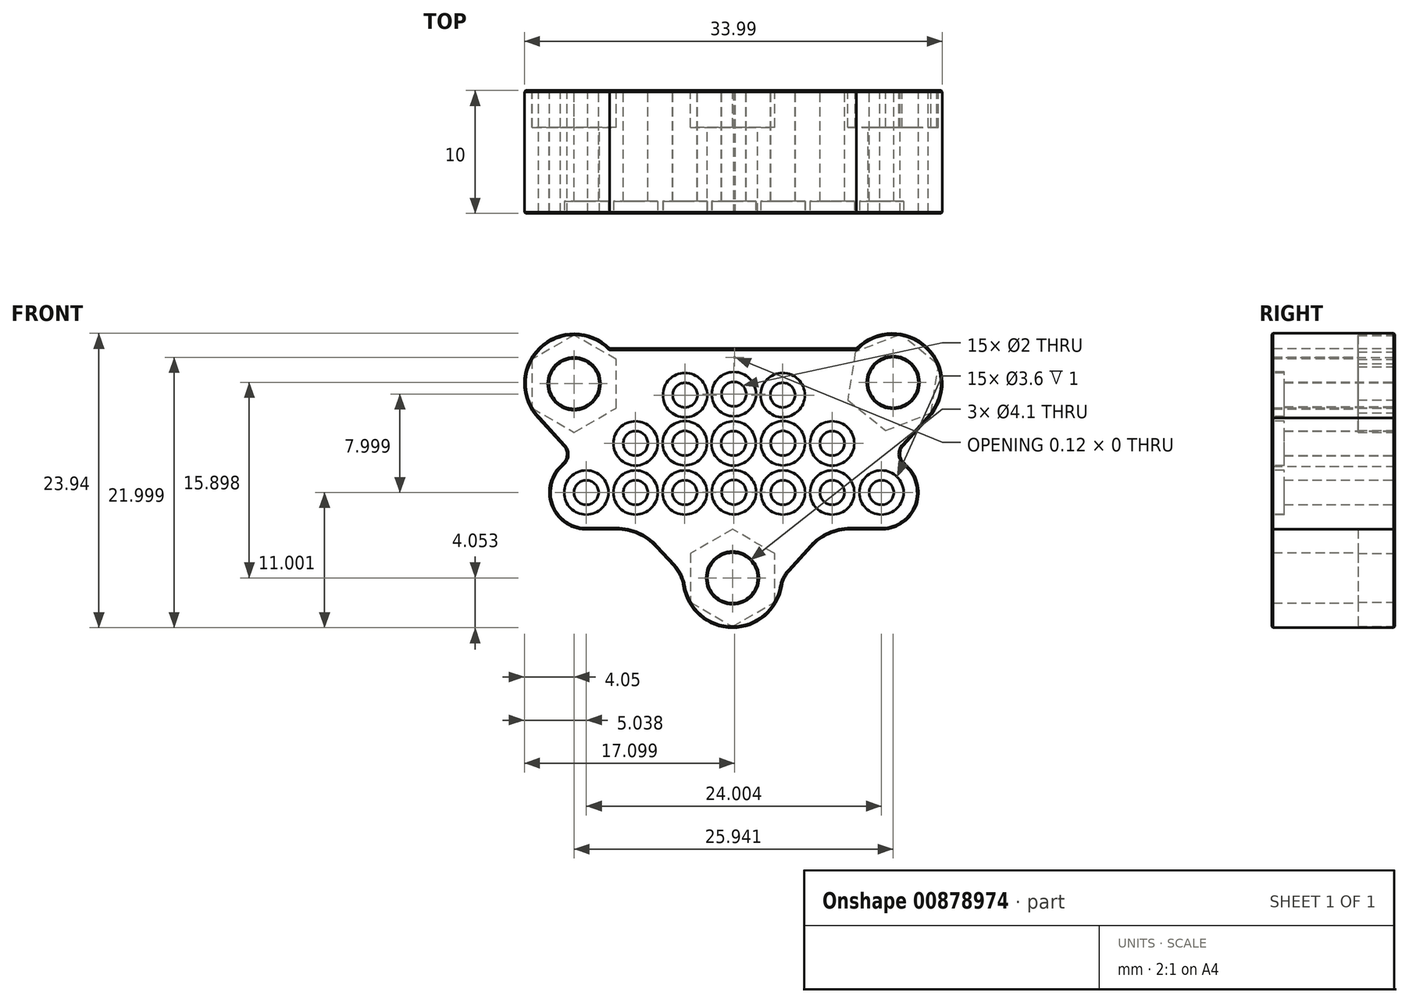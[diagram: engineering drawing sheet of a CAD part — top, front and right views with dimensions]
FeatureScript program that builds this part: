
annotation { "Feature Type Name" : "Feature", "Feature Type Description" : "" }
export const myFeature = defineFeature(function(context is Context, id is Id, definition is map)
    precondition{}
    {
        {
            var Q0;
            Q0=qCreatedBy(makeId("Front.planeOp"),FACE);
            var sketch = newSketch(context, id + "F0", { "sketchPlane" : qUnion([Q0])});
            skLineSegment(sketch, "E0", {"start": v(0, 0) * mm, "end": v(12, 0) * mm, "construction": true});
            skLineSegment(sketch, "E1.0", {"start": v(0, -4) * mm, "end": v(12, -4) * mm, "construction": true});
            skLineSegment(sketch, "E2", {"start": v(0, 4) * mm, "end": v(0, -4) * mm, "construction": true});
            skLineSegment(sketch, "E3.0", {"start": v(4, 4) * mm, "end": v(4, -4) * mm, "construction": true});
            skLineSegment(sketch, "E4.0", {"start": v(8, 4) * mm, "end": v(8, -4) * mm, "construction": true});
            skLineSegment(sketch, "E5.0", {"start": v(12, 0) * mm, "end": v(12, -4) * mm, "construction": true});
            skLineSegment(sketch, "E6.0", {"start": v(0, 4) * mm, "end": v(8, 4) * mm, "construction": true});
            skCircle(sketch, "E7", {"center": v(0, 4) * mm, "radius": 1 * mm});
            skCircle(sketch, "E8", {"center": v(3.97, 3.92) * mm, "radius": 1 * mm});
            skCircle(sketch, "E9", {"center": v(-0.03, 0) * mm, "radius": 1 * mm});
            skCircle(sketch, "E10", {"center": v(4, 0) * mm, "radius": 1 * mm});
            skCircle(sketch, "E11", {"center": v(8, 0) * mm, "radius": 1 * mm});
            skCircle(sketch, "E12", {"center": v(0, -3.98) * mm, "radius": 1 * mm});
            skCircle(sketch, "E13", {"center": v(4, -4) * mm, "radius": 1 * mm});
            skCircle(sketch, "E14", {"center": v(8, -4) * mm, "radius": 1 * mm});
            skCircle(sketch, "E15", {"center": v(12, -4) * mm, "radius": 1 * mm});
            skArc(sketch, "E16.0", {"start": v(11.88, -7) * mm, "mid": v(14.75, -5.2) * mm, "end": v(14.1, -1.86) * mm});
            skLineSegment(sketch, "E17", {"start": v(0, 7) * mm, "end": v(0.12, 7) * mm});
            skLineSegment(sketch, "E18", {"start": v(12.12, -7) * mm, "end": v(9.45, -7) * mm});
            skArc(sketch, "E19.trimOffspring", {"start": v(0.12, 7) * mm, "mid": v(0.06, 7) * mm, "end": v(0, 7) * mm});
            skCircle(sketch, "E20.MirrorC", {"center": v(-4, -4) * mm, "radius": 1 * mm});
            skCircle(sketch, "E21.MirrorC", {"center": v(-8, -4) * mm, "radius": 1 * mm});
            skCircle(sketch, "E22.MirrorC", {"center": v(-12, -4) * mm, "radius": 1 * mm});
            skLineSegment(sketch, "E23.MirrorCS", {"start": v(-4, 4) * mm, "end": v(-4, -4) * mm, "construction": true});
            skCircle(sketch, "E24.MirrorC", {"center": v(-4, 0) * mm, "radius": 1 * mm});
            skLineSegment(sketch, "E25.MirrorCS", {"start": v(-12, 0) * mm, "end": v(-12, -4) * mm, "construction": true});
            skLineSegment(sketch, "E26.MirrorCS", {"start": v(-8, 4) * mm, "end": v(-8, -4) * mm, "construction": true});
            skCircle(sketch, "E27.MirrorC", {"center": v(-3.97, 3.92) * mm, "radius": 1 * mm});
            skCircle(sketch, "E28.MirrorC", {"center": v(-8, 0) * mm, "radius": 1 * mm});
            skArc(sketch, "E29.MirrorCS", {"start": v(-11.88, -7) * mm, "mid": v(-14.75, -5.2) * mm, "end": v(-14.1, -1.86) * mm});
            skLineSegment(sketch, "E30.MirrorCS", {"start": v(-12.12, -7) * mm, "end": v(-9.54, -7) * mm});
            skPoint(sketch, "E31.orphan", {"position": v(3, -4.1) * mm});
            skPoint(sketch, "E32.0.end.orphan", {"position": v(3, -3.88) * mm});
            skPoint(sketch, "E33.MirrorCS.end.orphan", {"position": v(-3, -3.88) * mm});
            skPoint(sketch, "E33.MirrorCS.start.orphan", {"position": v(-3, -4.1) * mm});
            skLineSegment(sketch, "E34.0", {"start": v(12.1, -11) * mm, "end": v(0, -10.98) * mm});
            skCircle(sketch, "E35", {"center": v(-12.99, 4.85) * mm, "radius": 2.05 * mm});
            skCircle(sketch, "E36", {"center": v(12.95, 4.95) * mm, "radius": 2.05 * mm});
            skCircle(sketch, "E37", {"center": v(-0.1, -10.95) * mm, "radius": 2.05 * mm});
            skArc(sketch, "E38.0", {"start": v(-4.1, -11.59) * mm, "mid": v(-0.13, -15) * mm, "end": v(3.88, -11.63) * mm});
            skLineSegment(sketch, "E39", {"start": v(-10.1, 7.7) * mm, "end": v(9.97, 7.7) * mm});
            skLineSegment(sketch, "E40", {"start": v(-15.87, 2.02) * mm, "end": v(-13.82, -0.22) * mm});
            skLineSegment(sketch, "E41", {"start": v(4.5, -10.37) * mm, "end": v(6.32, -8.37) * mm});
            skLineSegment(sketch, "E42.trimOffspring", {"start": v(-13.84, -1.58) * mm, "end": v(-14.1, -1.86) * mm});
            skLineSegment(sketch, "E43.trimOffspring", {"start": v(-6.32, -8.4) * mm, "end": v(-4.88, -9.98) * mm});
            skArc(sketch, "E44.trimOffspring", {"start": v(-10.1, 7.7) * mm, "mid": v(-15.83, 7.75) * mm, "end": v(-15.87, 2.02) * mm});
            skPoint(sketch, "E45.MirrorCS.end.orphan", {"position": v(-4.03, 6.92) * mm});
            skPoint(sketch, "E45.MirrorCS.start.orphan", {"position": v(-6.26, 5.86) * mm});
            skPoint(sketch, "E46.MirrorCS.start.orphan", {"position": v(0, 7) * mm});
            skPoint(sketch, "E47.trimOffspring.end.orphan", {"position": v(4.03, 6.92) * mm});
            skPoint(sketch, "E48.orphan", {"position": v(6.26, 5.86) * mm});
            skArc(sketch, "E49.trimOffspring", {"start": v(15.81, 2.07) * mm, "mid": v(15.7, 7.8) * mm, "end": v(9.97, 7.7) * mm});
            skLineSegment(sketch, "E50.trimOffspring", {"start": v(13.8, -1.57) * mm, "end": v(14.1, -1.86) * mm});
            skLineSegment(sketch, "E51.trimOffspring", {"start": v(13.77, -0.18) * mm, "end": v(15.81, 2.07) * mm});
            skPoint(sketch, "E52.trimOffspring.end.orphan", {"position": v(0, -6.98) * mm});
            skPoint(sketch, "E53.0.start.orphan", {"position": v(-9.07, 8.7) * mm});
            skPoint(sketch, "E54.trimOffspring.end.orphan", {"position": v(-16.91, 1) * mm});
            skPoint(sketch, "E55.visualSharp", {"position": v(-13.2, -0.9) * mm});
            skArc(sketch, "E55.filletArc", {"start": v(-13.84, -1.58) * mm, "mid": v(-13.56, -0.9) * mm, "end": v(-13.82, -0.22) * mm});
            skPoint(sketch, "E56.visualSharp", {"position": v(-7.62, -6.99) * mm});
            skArc(sketch, "E56.filletArc", {"start": v(-6.32, -8.4) * mm, "mid": v(-7.78, -7.36) * mm, "end": v(-9.54, -7) * mm});
            skPoint(sketch, "E57.visualSharp", {"position": v(-4.15, -10.78) * mm});
            skArc(sketch, "E57.filletArc", {"start": v(-4.1, -11.59) * mm, "mid": v(-4.38, -10.73) * mm, "end": v(-4.88, -9.98) * mm});
            skPoint(sketch, "E58.visualSharp", {"position": v(13.12, -0.9) * mm});
            skArc(sketch, "E58.filletArc", {"start": v(13.77, -0.18) * mm, "mid": v(13.5, -0.88) * mm, "end": v(13.8, -1.57) * mm});
            skPoint(sketch, "E59.visualSharp", {"position": v(7.57, -6.99) * mm});
            skArc(sketch, "E59.filletArc", {"start": v(9.45, -7) * mm, "mid": v(7.73, -7.35) * mm, "end": v(6.32, -8.37) * mm});
            skPoint(sketch, "E60.visualSharp", {"position": v(3.94, -10.98) * mm});
            skArc(sketch, "E60.filletArc", {"start": v(4.5, -10.37) * mm, "mid": v(4.1, -10.96) * mm, "end": v(3.88, -11.63) * mm});
            skSolve(sketch);
        }
        {
            var Q0;
            Q0 = qSketchRegion(id + "F0", true);
            extrude(context, id + "F1", {"entities" : qUnion([Q0]), "depth" : 10 * mm, "offsetDistance" : 25 * mm});
        }
        {
            var Q0;
            Q0=makeQuery(id+"F1.opExtrude","CAP_FACE",FACE,{"disambiguationData":[OSD([sQuery(id+"F0.wireOp",EDGE,"E7"),sQuery(id+"F0.wireOp",EDGE,"E8"),sQuery(id+"F0.wireOp",EDGE,"E9"),sQuery(id+"F0.wireOp",EDGE,"E10"),sQuery(id+"F0.wireOp",EDGE,"E11"),sQuery(id+"F0.wireOp",EDGE,"E12"),sQuery(id+"F0.wireOp",EDGE,"E13"),sQuery(id+"F0.wireOp",EDGE,"E14"),sQuery(id+"F0.wireOp",EDGE,"E15"),sQuery(id+"F0.wireOp",EDGE,"E16.0"),sQuery(id+"F0.wireOp",EDGE,"E17"),sQuery(id+"F0.wireOp",EDGE,"E18"),sQuery(id+"F0.wireOp",EDGE,"E19.trimOffspring"),sQuery(id+"F0.wireOp",EDGE,"E20.MirrorC"),sQuery(id+"F0.wireOp",EDGE,"E21.MirrorC"),sQuery(id+"F0.wireOp",EDGE,"E22.MirrorC"),sQuery(id+"F0.wireOp",EDGE,"E24.MirrorC"),sQuery(id+"F0.wireOp",EDGE,"E27.MirrorC"),sQuery(id+"F0.wireOp",EDGE,"E28.MirrorC"),sQuery(id+"F0.wireOp",EDGE,"E29.MirrorCS"),sQuery(id+"F0.wireOp",EDGE,"E30.MirrorCS"),sQuery(id+"F0.wireOp",EDGE,"E35"),sQuery(id+"F0.wireOp",EDGE,"E36"),sQuery(id+"F0.wireOp",EDGE,"E37"),sQuery(id+"F0.wireOp",EDGE,"E38.0"),sQuery(id+"F0.wireOp",EDGE,"E39"),sQuery(id+"F0.wireOp",EDGE,"E40"),sQuery(id+"F0.wireOp",EDGE,"E41"),sQuery(id+"F0.wireOp",EDGE,"E42.trimOffspring"),sQuery(id+"F0.wireOp",EDGE,"E43.trimOffspring"),sQuery(id+"F0.wireOp",EDGE,"E44.trimOffspring"),sQuery(id+"F0.wireOp",EDGE,"E49.trimOffspring"),sQuery(id+"F0.wireOp",EDGE,"E50.trimOffspring"),sQuery(id+"F0.wireOp",EDGE,"E51.trimOffspring"),sQuery(id+"F0.wireOp",EDGE,"E55.filletArc"),sQuery(id+"F0.wireOp",EDGE,"E56.filletArc"),sQuery(id+"F0.wireOp",EDGE,"E57.filletArc"),sQuery(id+"F0.wireOp",EDGE,"E58.filletArc"),sQuery(id+"F0.wireOp",EDGE,"E59.filletArc"),sQuery(id+"F0.wireOp",EDGE,"E60.filletArc")])],"isStart":false});
            var sketch = newSketch(context, id + "F2", { "sketchPlane" : qUnion([Q0])});
            skCircle(sketch, "E61.0", {"center": v(-3.97, 3.92) * mm, "radius": 1.8 * mm});
            skLineSegment(sketch, "E62.0", {"start": v(9.78, -12) * mm, "end": v(11.8, -12) * mm});
            skLineSegment(sketch, "E62.1", {"start": v(8.65, -13.24) * mm, "end": v(9.78, -12) * mm});
            skArc(sketch, "E62.2", {"start": v(11.8, -12) * mm, "mid": v(18.5, -8.68) * mm, "end": v(19.53, -1.28) * mm});
            skArc(sketch, "E62.3", {"start": v(-8.93, -12.97) * mm, "mid": v(-0.25, -20) * mm, "end": v(8.65, -13.24) * mm});
            skLineSegment(sketch, "E62.4", {"start": v(-9.82, -12) * mm, "end": v(-8.93, -12.97) * mm});
            skLineSegment(sketch, "E62.5", {"start": v(-11.8, -12) * mm, "end": v(-9.82, -12) * mm});
            skArc(sketch, "E62.6", {"start": v(19.53, -1.28) * mm, "mid": v(19.96, 10.55) * mm, "end": v(8.31, 12.7) * mm});
            skLineSegment(sketch, "E62.7", {"start": v(8.31, 12.7) * mm, "end": v(-8.47, 12.7) * mm});
            skArc(sketch, "E62.8", {"start": v(-8.47, 12.7) * mm, "mid": v(-20.1, 10.46) * mm, "end": v(-19.56, -1.36) * mm});
            skArc(sketch, "E62.9", {"start": v(-19.56, -1.36) * mm, "mid": v(-18.46, -8.72) * mm, "end": v(-11.8, -12) * mm});
            skCircle(sketch, "E63.0", {"center": v(0, 4) * mm, "radius": 1.8 * mm});
            skCircle(sketch, "E64.0", {"center": v(3.97, 3.92) * mm, "radius": 1.8 * mm});
            skCircle(sketch, "E65.0", {"center": v(-8, 0) * mm, "radius": 1.8 * mm});
            skCircle(sketch, "E66.0", {"center": v(-4, 0) * mm, "radius": 1.8 * mm});
            skCircle(sketch, "E67.0", {"center": v(-0.03, 0) * mm, "radius": 1.8 * mm});
            skCircle(sketch, "E68.0", {"center": v(4, 0) * mm, "radius": 1.8 * mm});
            skCircle(sketch, "E69.0", {"center": v(8, 0) * mm, "radius": 1.8 * mm});
            skCircle(sketch, "E70.0", {"center": v(-12, -4) * mm, "radius": 1.8 * mm});
            skCircle(sketch, "E71.0", {"center": v(-8, -4) * mm, "radius": 1.8 * mm});
            skCircle(sketch, "E72.0", {"center": v(-4, -4) * mm, "radius": 1.8 * mm});
            skCircle(sketch, "E73.0", {"center": v(0, -3.98) * mm, "radius": 1.8 * mm});
            skCircle(sketch, "E74.0", {"center": v(4, -4) * mm, "radius": 1.8 * mm});
            skCircle(sketch, "E75.0", {"center": v(8, -4) * mm, "radius": 1.8 * mm});
            skCircle(sketch, "E76.0", {"center": v(12, -4) * mm, "radius": 1.8 * mm});
            skSolve(sketch);
        }
        {
            var Q0;
            Q0=makeQuery(id+"F2.imprint","IMPRINT",FACE,{"disambiguationData":[TD([[makeQuery(id+"F2.imprint","IMPRINT",EDGE,{"derivedFrom":sQuery(id+"F2.wireOp",EDGE,"E73.0")}),1.0]])]});
            var Q1;
            Q1=makeQuery(id+"F2.imprint","IMPRINT",FACE,{"disambiguationData":[TD([[makeQuery(id+"F2.imprint","IMPRINT",EDGE,{"derivedFrom":sQuery(id+"F2.wireOp",EDGE,"E76.0")}),1.0]])]});
            var Q2;
            Q2=makeQuery(id+"F2.imprint","IMPRINT",FACE,{"disambiguationData":[TD([[makeQuery(id+"F2.imprint","IMPRINT",EDGE,{"derivedFrom":sQuery(id+"F2.wireOp",EDGE,"E75.0")}),1.0]])]});
            var Q3;
            Q3=makeQuery(id+"F2.imprint","IMPRINT",FACE,{"disambiguationData":[TD([[makeQuery(id+"F2.imprint","IMPRINT",EDGE,{"derivedFrom":sQuery(id+"F2.wireOp",EDGE,"E74.0")}),1.0]])]});
            var Q4;
            Q4=makeQuery(id+"F2.imprint","IMPRINT",FACE,{"disambiguationData":[TD([[makeQuery(id+"F2.imprint","IMPRINT",EDGE,{"derivedFrom":sQuery(id+"F2.wireOp",EDGE,"E72.0")}),1.0]])]});
            var Q5;
            Q5=makeQuery(id+"F2.imprint","IMPRINT",FACE,{"disambiguationData":[TD([[makeQuery(id+"F2.imprint","IMPRINT",EDGE,{"derivedFrom":sQuery(id+"F2.wireOp",EDGE,"E71.0")}),1.0]])]});
            var Q6;
            Q6=makeQuery(id+"F2.imprint","IMPRINT",FACE,{"disambiguationData":[TD([[makeQuery(id+"F2.imprint","IMPRINT",EDGE,{"derivedFrom":sQuery(id+"F2.wireOp",EDGE,"E70.0")}),1.0]])]});
            var Q7;
            Q7=makeQuery(id+"F2.imprint","IMPRINT",FACE,{"disambiguationData":[TD([[makeQuery(id+"F2.imprint","IMPRINT",EDGE,{"derivedFrom":sQuery(id+"F2.wireOp",EDGE,"E65.0")}),1.0]])]});
            var Q8;
            Q8=makeQuery(id+"F2.imprint","IMPRINT",FACE,{"disambiguationData":[TD([[makeQuery(id+"F2.imprint","IMPRINT",EDGE,{"derivedFrom":sQuery(id+"F2.wireOp",EDGE,"E66.0")}),1.0]])]});
            var Q9;
            Q9=makeQuery(id+"F2.imprint","IMPRINT",FACE,{"disambiguationData":[TD([[makeQuery(id+"F2.imprint","IMPRINT",EDGE,{"derivedFrom":sQuery(id+"F2.wireOp",EDGE,"E67.0")}),1.0]])]});
            var Q10;
            Q10=makeQuery(id+"F2.imprint","IMPRINT",FACE,{"disambiguationData":[TD([[makeQuery(id+"F2.imprint","IMPRINT",EDGE,{"derivedFrom":sQuery(id+"F2.wireOp",EDGE,"E68.0")}),1.0]])]});
            var Q11;
            Q11=makeQuery(id+"F2.imprint","IMPRINT",FACE,{"disambiguationData":[TD([[makeQuery(id+"F2.imprint","IMPRINT",EDGE,{"derivedFrom":sQuery(id+"F2.wireOp",EDGE,"E69.0")}),1.0]])]});
            var Q12;
            Q12=makeQuery(id+"F2.imprint","IMPRINT",FACE,{"disambiguationData":[TD([[makeQuery(id+"F2.imprint","IMPRINT",EDGE,{"derivedFrom":sQuery(id+"F2.wireOp",EDGE,"E64.0")}),1.0]])]});
            var Q13;
            Q13=makeQuery(id+"F2.imprint","IMPRINT",FACE,{"disambiguationData":[TD([[makeQuery(id+"F2.imprint","IMPRINT",EDGE,{"derivedFrom":sQuery(id+"F2.wireOp",EDGE,"E63.0")}),1.0]])]});
            var Q14;
            Q14=makeQuery(id+"F2.imprint","IMPRINT",FACE,{"disambiguationData":[TD([[makeQuery(id+"F2.imprint","IMPRINT",EDGE,{"derivedFrom":sQuery(id+"F2.wireOp",EDGE,"E61.0")}),1.0]])]});
            extrude(context, id + "F3", {"entities" : qUnion([Q0, Q1, Q2, Q3, Q4, Q5, Q6, Q7, Q8, Q9, Q10, Q11, Q12, Q13, Q14]), "operationType" : NewBodyOperationType.REMOVE, "oppositeDirection" : true, "depth" : 1 * mm, "offsetDistance" : 25 * mm});
        }
        {
            var Q0;
            Q0=makeQuery(id+"F1.opExtrude","CAP_EDGE",EDGE,{"disambiguationData":[OSD([sQuery(id+"F0.wireOp",EDGE,"E39")])],"isStart":false});
            var Q1;
            Q1=makeQuery(id+"F1.opExtrude","CAP_EDGE",EDGE,{"disambiguationData":[OSD([sQuery(id+"F0.wireOp",EDGE,"E49.trimOffspring")])],"isStart":false});
            var Q2;
            Q2=makeQuery(id+"F1.opExtrude","CAP_EDGE",EDGE,{"disambiguationData":[OSD([sQuery(id+"F0.wireOp",EDGE,"E36")])],"isStart":false});
            var Q3;
            Q3=makeQuery(id+"F1.opExtrude","CAP_EDGE",EDGE,{"disambiguationData":[OSD([sQuery(id+"F0.wireOp",EDGE,"E51.trimOffspring")])],"isStart":false});
            var Q4;
            Q4=makeQuery(id+"F1.opExtrude","CAP_EDGE",EDGE,{"disambiguationData":[OSD([sQuery(id+"F0.wireOp",EDGE,"E58.filletArc")])],"isStart":false});
            var Q5;
            Q5=makeQuery(id+"F1.opExtrude","CAP_EDGE",EDGE,{"disambiguationData":[OSD([sQuery(id+"F0.wireOp",EDGE,"E50.trimOffspring")])],"isStart":false});
            var Q6;
            Q6=makeQuery(id+"F1.opExtrude","CAP_EDGE",EDGE,{"disambiguationData":[OSD([sQuery(id+"F0.wireOp",EDGE,"E16.0")])],"isStart":false});
            var Q7;
            Q7=makeQuery(id+"F1.opExtrude","CAP_EDGE",EDGE,{"disambiguationData":[OSD([sQuery(id+"F0.wireOp",EDGE,"E18")])],"isStart":false});
            var Q8;
            Q8=makeQuery(id+"F1.opExtrude","CAP_EDGE",EDGE,{"disambiguationData":[OSD([sQuery(id+"F0.wireOp",EDGE,"E59.filletArc")])],"isStart":false});
            var Q9;
            Q9=makeQuery(id+"F1.opExtrude","CAP_EDGE",EDGE,{"disambiguationData":[OSD([sQuery(id+"F0.wireOp",EDGE,"E41")])],"isStart":false});
            var Q10;
            Q10=makeQuery(id+"F1.opExtrude","CAP_EDGE",EDGE,{"disambiguationData":[OSD([sQuery(id+"F0.wireOp",EDGE,"E60.filletArc")])],"isStart":false});
            var Q11;
            Q11=makeQuery(id+"F1.opExtrude","CAP_EDGE",EDGE,{"disambiguationData":[OSD([sQuery(id+"F0.wireOp",EDGE,"E38.0")])],"isStart":false});
            var Q12;
            Q12=makeQuery(id+"F1.opExtrude","CAP_EDGE",EDGE,{"disambiguationData":[OSD([sQuery(id+"F0.wireOp",EDGE,"E57.filletArc")])],"isStart":false});
            var Q13;
            Q13=makeQuery(id+"F1.opExtrude","CAP_EDGE",EDGE,{"disambiguationData":[OSD([sQuery(id+"F0.wireOp",EDGE,"E43.trimOffspring")])],"isStart":false});
            var Q14;
            Q14=makeQuery(id+"F1.opExtrude","CAP_EDGE",EDGE,{"disambiguationData":[OSD([sQuery(id+"F0.wireOp",EDGE,"E56.filletArc")])],"isStart":false});
            var Q15;
            Q15=makeQuery(id+"F1.opExtrude","CAP_EDGE",EDGE,{"disambiguationData":[OSD([sQuery(id+"F0.wireOp",EDGE,"E30.MirrorCS")])],"isStart":false});
            var Q16;
            Q16=makeQuery(id+"F1.opExtrude","CAP_EDGE",EDGE,{"disambiguationData":[OSD([sQuery(id+"F0.wireOp",EDGE,"E37")])],"isStart":false});
            var Q17;
            Q17=makeQuery(id+"F1.opExtrude","CAP_EDGE",EDGE,{"disambiguationData":[OSD([sQuery(id+"F0.wireOp",EDGE,"E29.MirrorCS")])],"isStart":false});
            var Q18;
            Q18=makeQuery(id+"F1.opExtrude","CAP_EDGE",EDGE,{"disambiguationData":[OSD([sQuery(id+"F0.wireOp",EDGE,"E42.trimOffspring")])],"isStart":false});
            var Q19;
            Q19=makeQuery(id+"F1.opExtrude","CAP_EDGE",EDGE,{"disambiguationData":[OSD([sQuery(id+"F0.wireOp",EDGE,"E55.filletArc")])],"isStart":false});
            var Q20;
            Q20=makeQuery(id+"F1.opExtrude","CAP_EDGE",EDGE,{"disambiguationData":[OSD([sQuery(id+"F0.wireOp",EDGE,"E40")])],"isStart":false});
            var Q21;
            Q21=makeQuery(id+"F1.opExtrude","CAP_EDGE",EDGE,{"disambiguationData":[OSD([sQuery(id+"F0.wireOp",EDGE,"E44.trimOffspring")])],"isStart":false});
            var Q22;
            Q22=makeQuery(id+"F1.opExtrude","CAP_EDGE",EDGE,{"disambiguationData":[OSD([sQuery(id+"F0.wireOp",EDGE,"E35")])],"isStart":false});
            var Q23;
            Q23=makeQuery(id+"F3.boolean.opBoolean","COPY",EDGE,{"derivedFrom":makeQuery(id+"F3.opExtrude","CAP_EDGE",EDGE,{"disambiguationData":[OSD([sQuery(id+"F2.wireOp",EDGE,"E61.0")])],"isStart":true})});
            var Q24;
            Q24=makeQuery(id+"F3.boolean.opBoolean","COPY",EDGE,{"derivedFrom":makeQuery(id+"F3.opExtrude","CAP_EDGE",EDGE,{"disambiguationData":[OSD([sQuery(id+"F2.wireOp",EDGE,"E65.0")])],"isStart":true})});
            var Q25;
            Q25=makeQuery(id+"F3.boolean.opBoolean","COPY",EDGE,{"derivedFrom":makeQuery(id+"F3.opExtrude","CAP_EDGE",EDGE,{"disambiguationData":[OSD([sQuery(id+"F2.wireOp",EDGE,"E70.0")])],"isStart":true})});
            var Q26;
            Q26=makeQuery(id+"F3.boolean.opBoolean","COPY",EDGE,{"derivedFrom":makeQuery(id+"F3.opExtrude","CAP_EDGE",EDGE,{"disambiguationData":[OSD([sQuery(id+"F2.wireOp",EDGE,"E71.0")])],"isStart":true})});
            var Q27;
            Q27=makeQuery(id+"F3.boolean.opBoolean","COPY",EDGE,{"derivedFrom":makeQuery(id+"F3.opExtrude","CAP_EDGE",EDGE,{"disambiguationData":[OSD([sQuery(id+"F2.wireOp",EDGE,"E72.0")])],"isStart":true})});
            var Q28;
            Q28=makeQuery(id+"F3.boolean.opBoolean","COPY",EDGE,{"derivedFrom":makeQuery(id+"F3.opExtrude","CAP_EDGE",EDGE,{"disambiguationData":[OSD([sQuery(id+"F2.wireOp",EDGE,"E66.0")])],"isStart":true})});
            var Q29;
            Q29=makeQuery(id+"F3.boolean.opBoolean","COPY",EDGE,{"derivedFrom":makeQuery(id+"F3.opExtrude","CAP_EDGE",EDGE,{"disambiguationData":[OSD([sQuery(id+"F2.wireOp",EDGE,"E63.0")])],"isStart":true})});
            var Q30;
            Q30=makeQuery(id+"F3.boolean.opBoolean","COPY",EDGE,{"derivedFrom":makeQuery(id+"F3.opExtrude","CAP_EDGE",EDGE,{"disambiguationData":[OSD([sQuery(id+"F2.wireOp",EDGE,"E67.0")])],"isStart":true})});
            var Q31;
            Q31=makeQuery(id+"F3.boolean.opBoolean","COPY",EDGE,{"derivedFrom":makeQuery(id+"F3.opExtrude","CAP_EDGE",EDGE,{"disambiguationData":[OSD([sQuery(id+"F2.wireOp",EDGE,"E73.0")])],"isStart":true})});
            var Q32;
            Q32=makeQuery(id+"F3.boolean.opBoolean","COPY",EDGE,{"derivedFrom":makeQuery(id+"F3.opExtrude","CAP_EDGE",EDGE,{"disambiguationData":[OSD([sQuery(id+"F2.wireOp",EDGE,"E74.0")])],"isStart":true})});
            var Q33;
            Q33=makeQuery(id+"F3.boolean.opBoolean","COPY",EDGE,{"derivedFrom":makeQuery(id+"F3.opExtrude","CAP_EDGE",EDGE,{"disambiguationData":[OSD([sQuery(id+"F2.wireOp",EDGE,"E75.0")])],"isStart":true})});
            var Q34;
            Q34=makeQuery(id+"F3.boolean.opBoolean","COPY",EDGE,{"derivedFrom":makeQuery(id+"F3.opExtrude","CAP_EDGE",EDGE,{"disambiguationData":[OSD([sQuery(id+"F2.wireOp",EDGE,"E76.0")])],"isStart":true})});
            var Q35;
            Q35=makeQuery(id+"F3.boolean.opBoolean","COPY",EDGE,{"derivedFrom":makeQuery(id+"F3.opExtrude","CAP_EDGE",EDGE,{"disambiguationData":[OSD([sQuery(id+"F2.wireOp",EDGE,"E69.0")])],"isStart":true})});
            var Q36;
            Q36=makeQuery(id+"F3.boolean.opBoolean","COPY",EDGE,{"derivedFrom":makeQuery(id+"F3.opExtrude","CAP_EDGE",EDGE,{"disambiguationData":[OSD([sQuery(id+"F2.wireOp",EDGE,"E68.0")])],"isStart":true})});
            var Q37;
            Q37=makeQuery(id+"F3.boolean.opBoolean","COPY",EDGE,{"derivedFrom":makeQuery(id+"F3.opExtrude","CAP_EDGE",EDGE,{"disambiguationData":[OSD([sQuery(id+"F2.wireOp",EDGE,"E64.0")])],"isStart":true})});
            chamfer(context, id + "F4", {"entities" : qUnion([Q0, Q1, Q2, Q3, Q4, Q5, Q6, Q7, Q8, Q9, Q10, Q11, Q12, Q13, Q14, Q15, Q16, Q17, Q18, Q19, Q20, Q21, Q22, Q23, Q24, Q25, Q26, Q27, Q28, Q29, Q30, Q31, Q32, Q33, Q34, Q35, Q36, Q37]), "width" : 0.1 * mm, "tangentPropagation" : true});
        }
        {
            var Q0;
            Q0=makeQuery(id+"F1.opExtrude","CAP_EDGE",EDGE,{"disambiguationData":[OSD([sQuery(id+"F0.wireOp",EDGE,"E39")])],"isStart":true});
            var Q1;
            Q1=makeQuery(id+"F1.opExtrude","CAP_EDGE",EDGE,{"disambiguationData":[OSD([sQuery(id+"F0.wireOp",EDGE,"E44.trimOffspring")])],"isStart":true});
            var Q2;
            Q2=makeQuery(id+"F1.opExtrude","CAP_EDGE",EDGE,{"disambiguationData":[OSD([sQuery(id+"F0.wireOp",EDGE,"E40")])],"isStart":true});
            var Q3;
            Q3=makeQuery(id+"F1.opExtrude","CAP_EDGE",EDGE,{"disambiguationData":[OSD([sQuery(id+"F0.wireOp",EDGE,"E35")])],"isStart":true});
            var Q4;
            Q4=makeQuery(id+"F1.opExtrude","CAP_EDGE",EDGE,{"disambiguationData":[OSD([sQuery(id+"F0.wireOp",EDGE,"E36")])],"isStart":true});
            var Q5;
            Q5=makeQuery(id+"F1.opExtrude","CAP_EDGE",EDGE,{"disambiguationData":[OSD([sQuery(id+"F0.wireOp",EDGE,"E37")])],"isStart":true});
            var Q6;
            Q6=makeQuery(id+"F1.opExtrude","CAP_EDGE",EDGE,{"disambiguationData":[OSD([sQuery(id+"F0.wireOp",EDGE,"E29.MirrorCS")])],"isStart":true});
            var Q7;
            Q7=makeQuery(id+"F1.opExtrude","CAP_EDGE",EDGE,{"disambiguationData":[OSD([sQuery(id+"F0.wireOp",EDGE,"E55.filletArc")])],"isStart":true});
            var Q8;
            Q8=makeQuery(id+"F1.opExtrude","CAP_EDGE",EDGE,{"disambiguationData":[OSD([sQuery(id+"F0.wireOp",EDGE,"E30.MirrorCS")])],"isStart":true});
            var Q9;
            Q9=makeQuery(id+"F1.opExtrude","CAP_EDGE",EDGE,{"disambiguationData":[OSD([sQuery(id+"F0.wireOp",EDGE,"E56.filletArc")])],"isStart":true});
            var Q10;
            Q10=makeQuery(id+"F1.opExtrude","CAP_EDGE",EDGE,{"disambiguationData":[OSD([sQuery(id+"F0.wireOp",EDGE,"E43.trimOffspring")])],"isStart":true});
            var Q11;
            Q11=makeQuery(id+"F1.opExtrude","CAP_EDGE",EDGE,{"disambiguationData":[OSD([sQuery(id+"F0.wireOp",EDGE,"E57.filletArc")])],"isStart":true});
            var Q12;
            Q12=makeQuery(id+"F1.opExtrude","CAP_EDGE",EDGE,{"disambiguationData":[OSD([sQuery(id+"F0.wireOp",EDGE,"E38.0")])],"isStart":true});
            var Q13;
            Q13=makeQuery(id+"F1.opExtrude","CAP_EDGE",EDGE,{"disambiguationData":[OSD([sQuery(id+"F0.wireOp",EDGE,"E49.trimOffspring")])],"isStart":true});
            var Q14;
            Q14=makeQuery(id+"F1.opExtrude","CAP_EDGE",EDGE,{"disambiguationData":[OSD([sQuery(id+"F0.wireOp",EDGE,"E51.trimOffspring")])],"isStart":true});
            var Q15;
            Q15=makeQuery(id+"F1.opExtrude","CAP_EDGE",EDGE,{"disambiguationData":[OSD([sQuery(id+"F0.wireOp",EDGE,"E58.filletArc")])],"isStart":true});
            var Q16;
            Q16=makeQuery(id+"F1.opExtrude","CAP_EDGE",EDGE,{"disambiguationData":[OSD([sQuery(id+"F0.wireOp",EDGE,"E16.0")])],"isStart":true});
            var Q17;
            Q17=makeQuery(id+"F1.opExtrude","CAP_EDGE",EDGE,{"disambiguationData":[OSD([sQuery(id+"F0.wireOp",EDGE,"E18")])],"isStart":true});
            var Q18;
            Q18=makeQuery(id+"F1.opExtrude","CAP_EDGE",EDGE,{"disambiguationData":[OSD([sQuery(id+"F0.wireOp",EDGE,"E59.filletArc")])],"isStart":true});
            var Q19;
            Q19=makeQuery(id+"F1.opExtrude","CAP_EDGE",EDGE,{"disambiguationData":[OSD([sQuery(id+"F0.wireOp",EDGE,"E50.trimOffspring")])],"isStart":true});
            var Q20;
            Q20=makeQuery(id+"F1.opExtrude","CAP_EDGE",EDGE,{"disambiguationData":[OSD([sQuery(id+"F0.wireOp",EDGE,"E41")])],"isStart":true});
            var Q21;
            Q21=makeQuery(id+"F1.opExtrude","CAP_EDGE",EDGE,{"disambiguationData":[OSD([sQuery(id+"F0.wireOp",EDGE,"E60.filletArc")])],"isStart":true});
            chamfer(context, id + "F5", {"entities" : qUnion([Q0, Q1, Q2, Q3, Q4, Q5, Q6, Q7, Q8, Q9, Q10, Q11, Q12, Q13, Q14, Q15, Q16, Q17, Q18, Q19, Q20, Q21]), "width" : 0.1 * mm, "tangentPropagation" : true});
        }
        {
            var Q0;
            Q0=makeQuery(id+"F1.opExtrude","CAP_FACE",FACE,{"disambiguationData":[OSD([sQuery(id+"F0.wireOp",EDGE,"E7"),sQuery(id+"F0.wireOp",EDGE,"E8"),sQuery(id+"F0.wireOp",EDGE,"E9"),sQuery(id+"F0.wireOp",EDGE,"E10"),sQuery(id+"F0.wireOp",EDGE,"E11"),sQuery(id+"F0.wireOp",EDGE,"E12"),sQuery(id+"F0.wireOp",EDGE,"E13"),sQuery(id+"F0.wireOp",EDGE,"E14"),sQuery(id+"F0.wireOp",EDGE,"E15"),sQuery(id+"F0.wireOp",EDGE,"E16.0"),sQuery(id+"F0.wireOp",EDGE,"E17"),sQuery(id+"F0.wireOp",EDGE,"E18"),sQuery(id+"F0.wireOp",EDGE,"E19.trimOffspring"),sQuery(id+"F0.wireOp",EDGE,"E20.MirrorC"),sQuery(id+"F0.wireOp",EDGE,"E21.MirrorC"),sQuery(id+"F0.wireOp",EDGE,"E22.MirrorC"),sQuery(id+"F0.wireOp",EDGE,"E24.MirrorC"),sQuery(id+"F0.wireOp",EDGE,"E27.MirrorC"),sQuery(id+"F0.wireOp",EDGE,"E28.MirrorC"),sQuery(id+"F0.wireOp",EDGE,"E29.MirrorCS"),sQuery(id+"F0.wireOp",EDGE,"E30.MirrorCS"),sQuery(id+"F0.wireOp",EDGE,"E35"),sQuery(id+"F0.wireOp",EDGE,"E36"),sQuery(id+"F0.wireOp",EDGE,"E37"),sQuery(id+"F0.wireOp",EDGE,"E38.0"),sQuery(id+"F0.wireOp",EDGE,"E39"),sQuery(id+"F0.wireOp",EDGE,"E40"),sQuery(id+"F0.wireOp",EDGE,"E41"),sQuery(id+"F0.wireOp",EDGE,"E42.trimOffspring"),sQuery(id+"F0.wireOp",EDGE,"E43.trimOffspring"),sQuery(id+"F0.wireOp",EDGE,"E44.trimOffspring"),sQuery(id+"F0.wireOp",EDGE,"E49.trimOffspring"),sQuery(id+"F0.wireOp",EDGE,"E50.trimOffspring"),sQuery(id+"F0.wireOp",EDGE,"E51.trimOffspring"),sQuery(id+"F0.wireOp",EDGE,"E55.filletArc"),sQuery(id+"F0.wireOp",EDGE,"E56.filletArc"),sQuery(id+"F0.wireOp",EDGE,"E57.filletArc"),sQuery(id+"F0.wireOp",EDGE,"E58.filletArc"),sQuery(id+"F0.wireOp",EDGE,"E59.filletArc"),sQuery(id+"F0.wireOp",EDGE,"E60.filletArc")])],"isStart":true});
            var sketch = newSketch(context, id + "F6", { "sketchPlane" : qUnion([Q0])});
            skCircle(sketch, "E77.cCircle", {"center": v(-12.95, 4.95) * mm, "radius": 3.43 * mm, "construction": true});
            skLineSegment(sketch, "E77.0", {"start": v(-9.26, 3.53) * mm, "end": v(-12.33, 1.05) * mm});
            skLineSegment(sketch, "E77.1", {"start": v(-12.33, 1.05) * mm, "end": v(-16.03, 2.46) * mm});
            skLineSegment(sketch, "E77.2", {"start": v(-16.03, 2.46) * mm, "end": v(-16.64, 6.37) * mm});
            skLineSegment(sketch, "E77.3", {"start": v(-16.64, 6.37) * mm, "end": v(-13.57, 8.86) * mm});
            skLineSegment(sketch, "E77.4", {"start": v(-13.57, 8.86) * mm, "end": v(-9.88, 7.44) * mm});
            skLineSegment(sketch, "E77.5", {"start": v(-9.88, 7.44) * mm, "end": v(-9.26, 3.53) * mm});
            skPoint(sketch, "E77.0.midPoint", {"position": v(-10.8, 2.29) * mm});
            skCircle(sketch, "E78.cCircle", {"center": v(12.99, 4.85) * mm, "radius": 3.43 * mm, "construction": true});
            skLineSegment(sketch, "E78.0", {"start": v(16.41, 2.87) * mm, "end": v(13, 0.9) * mm});
            skLineSegment(sketch, "E78.1", {"start": v(13, 0.9) * mm, "end": v(9.56, 2.87) * mm});
            skLineSegment(sketch, "E78.2", {"start": v(9.56, 2.87) * mm, "end": v(9.56, 6.83) * mm});
            skLineSegment(sketch, "E78.3", {"start": v(9.56, 6.83) * mm, "end": v(12.99, 8.8) * mm});
            skLineSegment(sketch, "E78.4", {"start": v(12.99, 8.8) * mm, "end": v(16.41, 6.83) * mm});
            skLineSegment(sketch, "E78.5", {"start": v(16.41, 6.83) * mm, "end": v(16.41, 2.87) * mm});
            skPoint(sketch, "E78.0.midPoint", {"position": v(14.7, 1.88) * mm});
            skCircle(sketch, "E79.cCircle", {"center": v(0.1, -10.95) * mm, "radius": 3.43 * mm, "construction": true});
            skLineSegment(sketch, "E79.0", {"start": v(3.53, -8.97) * mm, "end": v(3.53, -12.92) * mm});
            skLineSegment(sketch, "E79.1", {"start": v(3.53, -12.92) * mm, "end": v(0.1, -14.9) * mm});
            skLineSegment(sketch, "E79.2", {"start": v(0.1, -14.9) * mm, "end": v(-3.32, -12.92) * mm});
            skLineSegment(sketch, "E79.3", {"start": v(-3.32, -12.92) * mm, "end": v(-3.32, -8.97) * mm});
            skLineSegment(sketch, "E79.4", {"start": v(-3.32, -8.97) * mm, "end": v(0.1, -7) * mm});
            skLineSegment(sketch, "E79.5", {"start": v(0.1, -7) * mm, "end": v(3.53, -8.97) * mm});
            skPoint(sketch, "E79.0.midPoint", {"position": v(3.53, -10.95) * mm});
            skSolve(sketch);
        }
        {
            var Q0;
            {var subQ11=sQuery(id+"F6.wireOp",EDGE,"E77.0");Q0=makeQuery(id+"F6.imprint","IMPRINT",FACE,{"disambiguationData":[TD([[makeQuery(id+"F6.imprint","IMPRINT",EDGE,{"derivedFrom":subQ11}),-1.0]])]});}
            var Q1;
            {var subQ0=sQuery(id+"F0.wireOp",EDGE,"E36");Q1=makeQuery(id+"F6.imprint","IMPRINT",FACE,{"disambiguationData":[TD([[makeQuery(id+"F6.imprint","IMPRINT",EDGE,{"derivedFrom":makeQuery(id+"F5.opChamfer","BLEND_EDGE",EDGE,{"blendedFrom":[makeQuery(id+"F1.opExtrude","CAP_EDGE",EDGE,{"disambiguationData":[OSD([subQ0])],"isStart":true}),makeQuery(id+"F1.opExtrude","CAP_FACE",FACE,{"disambiguationData":[OSD([sQuery(id+"F0.wireOp",EDGE,"E7"),sQuery(id+"F0.wireOp",EDGE,"E8"),sQuery(id+"F0.wireOp",EDGE,"E9"),sQuery(id+"F0.wireOp",EDGE,"E10"),sQuery(id+"F0.wireOp",EDGE,"E11"),sQuery(id+"F0.wireOp",EDGE,"E12"),sQuery(id+"F0.wireOp",EDGE,"E13"),sQuery(id+"F0.wireOp",EDGE,"E14"),sQuery(id+"F0.wireOp",EDGE,"E15"),sQuery(id+"F0.wireOp",EDGE,"E16.0"),sQuery(id+"F0.wireOp",EDGE,"E17"),sQuery(id+"F0.wireOp",EDGE,"E18"),sQuery(id+"F0.wireOp",EDGE,"E19.trimOffspring"),sQuery(id+"F0.wireOp",EDGE,"E20.MirrorC"),sQuery(id+"F0.wireOp",EDGE,"E21.MirrorC"),sQuery(id+"F0.wireOp",EDGE,"E22.MirrorC"),sQuery(id+"F0.wireOp",EDGE,"E24.MirrorC"),sQuery(id+"F0.wireOp",EDGE,"E27.MirrorC"),sQuery(id+"F0.wireOp",EDGE,"E28.MirrorC"),sQuery(id+"F0.wireOp",EDGE,"E29.MirrorCS"),sQuery(id+"F0.wireOp",EDGE,"E30.MirrorCS"),sQuery(id+"F0.wireOp",EDGE,"E35"),subQ0,sQuery(id+"F0.wireOp",EDGE,"E37"),sQuery(id+"F0.wireOp",EDGE,"E38.0"),sQuery(id+"F0.wireOp",EDGE,"E39"),sQuery(id+"F0.wireOp",EDGE,"E40"),sQuery(id+"F0.wireOp",EDGE,"E41"),sQuery(id+"F0.wireOp",EDGE,"E42.trimOffspring"),sQuery(id+"F0.wireOp",EDGE,"E43.trimOffspring"),sQuery(id+"F0.wireOp",EDGE,"E44.trimOffspring"),sQuery(id+"F0.wireOp",EDGE,"E49.trimOffspring"),sQuery(id+"F0.wireOp",EDGE,"E50.trimOffspring"),sQuery(id+"F0.wireOp",EDGE,"E51.trimOffspring"),sQuery(id+"F0.wireOp",EDGE,"E55.filletArc"),sQuery(id+"F0.wireOp",EDGE,"E56.filletArc"),sQuery(id+"F0.wireOp",EDGE,"E57.filletArc"),sQuery(id+"F0.wireOp",EDGE,"E58.filletArc"),sQuery(id+"F0.wireOp",EDGE,"E59.filletArc"),sQuery(id+"F0.wireOp",EDGE,"E60.filletArc")])],"isStart":true})],"blendedInto":[makeQuery(id+"F1.opExtrude","CAP_FACE",FACE,{"disambiguationData":[OSD([sQuery(id+"F0.wireOp",EDGE,"E7"),sQuery(id+"F0.wireOp",EDGE,"E8"),sQuery(id+"F0.wireOp",EDGE,"E9"),sQuery(id+"F0.wireOp",EDGE,"E10"),sQuery(id+"F0.wireOp",EDGE,"E11"),sQuery(id+"F0.wireOp",EDGE,"E12"),sQuery(id+"F0.wireOp",EDGE,"E13"),sQuery(id+"F0.wireOp",EDGE,"E14"),sQuery(id+"F0.wireOp",EDGE,"E15"),sQuery(id+"F0.wireOp",EDGE,"E16.0"),sQuery(id+"F0.wireOp",EDGE,"E17"),sQuery(id+"F0.wireOp",EDGE,"E18"),sQuery(id+"F0.wireOp",EDGE,"E19.trimOffspring"),sQuery(id+"F0.wireOp",EDGE,"E20.MirrorC"),sQuery(id+"F0.wireOp",EDGE,"E21.MirrorC"),sQuery(id+"F0.wireOp",EDGE,"E22.MirrorC"),sQuery(id+"F0.wireOp",EDGE,"E24.MirrorC"),sQuery(id+"F0.wireOp",EDGE,"E27.MirrorC"),sQuery(id+"F0.wireOp",EDGE,"E28.MirrorC"),sQuery(id+"F0.wireOp",EDGE,"E29.MirrorCS"),sQuery(id+"F0.wireOp",EDGE,"E30.MirrorCS"),sQuery(id+"F0.wireOp",EDGE,"E35"),subQ0,sQuery(id+"F0.wireOp",EDGE,"E37"),sQuery(id+"F0.wireOp",EDGE,"E38.0"),sQuery(id+"F0.wireOp",EDGE,"E39"),sQuery(id+"F0.wireOp",EDGE,"E40"),sQuery(id+"F0.wireOp",EDGE,"E41"),sQuery(id+"F0.wireOp",EDGE,"E42.trimOffspring"),sQuery(id+"F0.wireOp",EDGE,"E43.trimOffspring"),sQuery(id+"F0.wireOp",EDGE,"E44.trimOffspring"),sQuery(id+"F0.wireOp",EDGE,"E49.trimOffspring"),sQuery(id+"F0.wireOp",EDGE,"E50.trimOffspring"),sQuery(id+"F0.wireOp",EDGE,"E51.trimOffspring"),sQuery(id+"F0.wireOp",EDGE,"E55.filletArc"),sQuery(id+"F0.wireOp",EDGE,"E56.filletArc"),sQuery(id+"F0.wireOp",EDGE,"E57.filletArc"),sQuery(id+"F0.wireOp",EDGE,"E58.filletArc"),sQuery(id+"F0.wireOp",EDGE,"E59.filletArc"),sQuery(id+"F0.wireOp",EDGE,"E60.filletArc")])],"isStart":true})]})}),-1.0]])]});}
            var Q2;
            {var subQ1=sQuery(id+"F6.wireOp",EDGE,"E78.1");Q2=makeQuery(id+"F6.imprint","IMPRINT",FACE,{"disambiguationData":[TD([[makeQuery(id+"F6.imprint","IMPRINT",EDGE,{"derivedFrom":subQ1}),-1.0]])]});}
            var Q3;
            {var subQ0=sQuery(id+"F0.wireOp",EDGE,"E35");Q3=makeQuery(id+"F6.imprint","IMPRINT",FACE,{"disambiguationData":[TD([[makeQuery(id+"F6.imprint","IMPRINT",EDGE,{"derivedFrom":makeQuery(id+"F5.opChamfer","BLEND_EDGE",EDGE,{"blendedFrom":[makeQuery(id+"F1.opExtrude","CAP_EDGE",EDGE,{"disambiguationData":[OSD([subQ0])],"isStart":true}),makeQuery(id+"F1.opExtrude","CAP_FACE",FACE,{"disambiguationData":[OSD([sQuery(id+"F0.wireOp",EDGE,"E7"),sQuery(id+"F0.wireOp",EDGE,"E8"),sQuery(id+"F0.wireOp",EDGE,"E9"),sQuery(id+"F0.wireOp",EDGE,"E10"),sQuery(id+"F0.wireOp",EDGE,"E11"),sQuery(id+"F0.wireOp",EDGE,"E12"),sQuery(id+"F0.wireOp",EDGE,"E13"),sQuery(id+"F0.wireOp",EDGE,"E14"),sQuery(id+"F0.wireOp",EDGE,"E15"),sQuery(id+"F0.wireOp",EDGE,"E16.0"),sQuery(id+"F0.wireOp",EDGE,"E17"),sQuery(id+"F0.wireOp",EDGE,"E18"),sQuery(id+"F0.wireOp",EDGE,"E19.trimOffspring"),sQuery(id+"F0.wireOp",EDGE,"E20.MirrorC"),sQuery(id+"F0.wireOp",EDGE,"E21.MirrorC"),sQuery(id+"F0.wireOp",EDGE,"E22.MirrorC"),sQuery(id+"F0.wireOp",EDGE,"E24.MirrorC"),sQuery(id+"F0.wireOp",EDGE,"E27.MirrorC"),sQuery(id+"F0.wireOp",EDGE,"E28.MirrorC"),sQuery(id+"F0.wireOp",EDGE,"E29.MirrorCS"),sQuery(id+"F0.wireOp",EDGE,"E30.MirrorCS"),subQ0,sQuery(id+"F0.wireOp",EDGE,"E36"),sQuery(id+"F0.wireOp",EDGE,"E37"),sQuery(id+"F0.wireOp",EDGE,"E38.0"),sQuery(id+"F0.wireOp",EDGE,"E39"),sQuery(id+"F0.wireOp",EDGE,"E40"),sQuery(id+"F0.wireOp",EDGE,"E41"),sQuery(id+"F0.wireOp",EDGE,"E42.trimOffspring"),sQuery(id+"F0.wireOp",EDGE,"E43.trimOffspring"),sQuery(id+"F0.wireOp",EDGE,"E44.trimOffspring"),sQuery(id+"F0.wireOp",EDGE,"E49.trimOffspring"),sQuery(id+"F0.wireOp",EDGE,"E50.trimOffspring"),sQuery(id+"F0.wireOp",EDGE,"E51.trimOffspring"),sQuery(id+"F0.wireOp",EDGE,"E55.filletArc"),sQuery(id+"F0.wireOp",EDGE,"E56.filletArc"),sQuery(id+"F0.wireOp",EDGE,"E57.filletArc"),sQuery(id+"F0.wireOp",EDGE,"E58.filletArc"),sQuery(id+"F0.wireOp",EDGE,"E59.filletArc"),sQuery(id+"F0.wireOp",EDGE,"E60.filletArc")])],"isStart":true})],"blendedInto":[makeQuery(id+"F1.opExtrude","CAP_FACE",FACE,{"disambiguationData":[OSD([sQuery(id+"F0.wireOp",EDGE,"E7"),sQuery(id+"F0.wireOp",EDGE,"E8"),sQuery(id+"F0.wireOp",EDGE,"E9"),sQuery(id+"F0.wireOp",EDGE,"E10"),sQuery(id+"F0.wireOp",EDGE,"E11"),sQuery(id+"F0.wireOp",EDGE,"E12"),sQuery(id+"F0.wireOp",EDGE,"E13"),sQuery(id+"F0.wireOp",EDGE,"E14"),sQuery(id+"F0.wireOp",EDGE,"E15"),sQuery(id+"F0.wireOp",EDGE,"E16.0"),sQuery(id+"F0.wireOp",EDGE,"E17"),sQuery(id+"F0.wireOp",EDGE,"E18"),sQuery(id+"F0.wireOp",EDGE,"E19.trimOffspring"),sQuery(id+"F0.wireOp",EDGE,"E20.MirrorC"),sQuery(id+"F0.wireOp",EDGE,"E21.MirrorC"),sQuery(id+"F0.wireOp",EDGE,"E22.MirrorC"),sQuery(id+"F0.wireOp",EDGE,"E24.MirrorC"),sQuery(id+"F0.wireOp",EDGE,"E27.MirrorC"),sQuery(id+"F0.wireOp",EDGE,"E28.MirrorC"),sQuery(id+"F0.wireOp",EDGE,"E29.MirrorCS"),sQuery(id+"F0.wireOp",EDGE,"E30.MirrorCS"),subQ0,sQuery(id+"F0.wireOp",EDGE,"E36"),sQuery(id+"F0.wireOp",EDGE,"E37"),sQuery(id+"F0.wireOp",EDGE,"E38.0"),sQuery(id+"F0.wireOp",EDGE,"E39"),sQuery(id+"F0.wireOp",EDGE,"E40"),sQuery(id+"F0.wireOp",EDGE,"E41"),sQuery(id+"F0.wireOp",EDGE,"E42.trimOffspring"),sQuery(id+"F0.wireOp",EDGE,"E43.trimOffspring"),sQuery(id+"F0.wireOp",EDGE,"E44.trimOffspring"),sQuery(id+"F0.wireOp",EDGE,"E49.trimOffspring"),sQuery(id+"F0.wireOp",EDGE,"E50.trimOffspring"),sQuery(id+"F0.wireOp",EDGE,"E51.trimOffspring"),sQuery(id+"F0.wireOp",EDGE,"E55.filletArc"),sQuery(id+"F0.wireOp",EDGE,"E56.filletArc"),sQuery(id+"F0.wireOp",EDGE,"E57.filletArc"),sQuery(id+"F0.wireOp",EDGE,"E58.filletArc"),sQuery(id+"F0.wireOp",EDGE,"E59.filletArc"),sQuery(id+"F0.wireOp",EDGE,"E60.filletArc")])],"isStart":true})]})}),-1.0]])]});}
            var Q4;
            {var subQ0=sQuery(id+"F6.wireOp",EDGE,"E79.4");Q4=makeQuery(id+"F6.imprint","IMPRINT",FACE,{"disambiguationData":[TD([[makeQuery(id+"F6.imprint","IMPRINT",EDGE,{"derivedFrom":subQ0}),-1.0]])]});}
            var Q5;
            {var subQ0=sQuery(id+"F0.wireOp",EDGE,"E37");Q5=makeQuery(id+"F6.imprint","IMPRINT",FACE,{"disambiguationData":[TD([[makeQuery(id+"F6.imprint","IMPRINT",EDGE,{"derivedFrom":makeQuery(id+"F5.opChamfer","BLEND_EDGE",EDGE,{"blendedFrom":[makeQuery(id+"F1.opExtrude","CAP_EDGE",EDGE,{"disambiguationData":[OSD([subQ0])],"isStart":true}),makeQuery(id+"F1.opExtrude","CAP_FACE",FACE,{"disambiguationData":[OSD([sQuery(id+"F0.wireOp",EDGE,"E7"),sQuery(id+"F0.wireOp",EDGE,"E8"),sQuery(id+"F0.wireOp",EDGE,"E9"),sQuery(id+"F0.wireOp",EDGE,"E10"),sQuery(id+"F0.wireOp",EDGE,"E11"),sQuery(id+"F0.wireOp",EDGE,"E12"),sQuery(id+"F0.wireOp",EDGE,"E13"),sQuery(id+"F0.wireOp",EDGE,"E14"),sQuery(id+"F0.wireOp",EDGE,"E15"),sQuery(id+"F0.wireOp",EDGE,"E16.0"),sQuery(id+"F0.wireOp",EDGE,"E17"),sQuery(id+"F0.wireOp",EDGE,"E18"),sQuery(id+"F0.wireOp",EDGE,"E19.trimOffspring"),sQuery(id+"F0.wireOp",EDGE,"E20.MirrorC"),sQuery(id+"F0.wireOp",EDGE,"E21.MirrorC"),sQuery(id+"F0.wireOp",EDGE,"E22.MirrorC"),sQuery(id+"F0.wireOp",EDGE,"E24.MirrorC"),sQuery(id+"F0.wireOp",EDGE,"E27.MirrorC"),sQuery(id+"F0.wireOp",EDGE,"E28.MirrorC"),sQuery(id+"F0.wireOp",EDGE,"E29.MirrorCS"),sQuery(id+"F0.wireOp",EDGE,"E30.MirrorCS"),sQuery(id+"F0.wireOp",EDGE,"E35"),sQuery(id+"F0.wireOp",EDGE,"E36"),subQ0,sQuery(id+"F0.wireOp",EDGE,"E38.0"),sQuery(id+"F0.wireOp",EDGE,"E39"),sQuery(id+"F0.wireOp",EDGE,"E40"),sQuery(id+"F0.wireOp",EDGE,"E41"),sQuery(id+"F0.wireOp",EDGE,"E42.trimOffspring"),sQuery(id+"F0.wireOp",EDGE,"E43.trimOffspring"),sQuery(id+"F0.wireOp",EDGE,"E44.trimOffspring"),sQuery(id+"F0.wireOp",EDGE,"E49.trimOffspring"),sQuery(id+"F0.wireOp",EDGE,"E50.trimOffspring"),sQuery(id+"F0.wireOp",EDGE,"E51.trimOffspring"),sQuery(id+"F0.wireOp",EDGE,"E55.filletArc"),sQuery(id+"F0.wireOp",EDGE,"E56.filletArc"),sQuery(id+"F0.wireOp",EDGE,"E57.filletArc"),sQuery(id+"F0.wireOp",EDGE,"E58.filletArc"),sQuery(id+"F0.wireOp",EDGE,"E59.filletArc"),sQuery(id+"F0.wireOp",EDGE,"E60.filletArc")])],"isStart":true})],"blendedInto":[makeQuery(id+"F1.opExtrude","CAP_FACE",FACE,{"disambiguationData":[OSD([sQuery(id+"F0.wireOp",EDGE,"E7"),sQuery(id+"F0.wireOp",EDGE,"E8"),sQuery(id+"F0.wireOp",EDGE,"E9"),sQuery(id+"F0.wireOp",EDGE,"E10"),sQuery(id+"F0.wireOp",EDGE,"E11"),sQuery(id+"F0.wireOp",EDGE,"E12"),sQuery(id+"F0.wireOp",EDGE,"E13"),sQuery(id+"F0.wireOp",EDGE,"E14"),sQuery(id+"F0.wireOp",EDGE,"E15"),sQuery(id+"F0.wireOp",EDGE,"E16.0"),sQuery(id+"F0.wireOp",EDGE,"E17"),sQuery(id+"F0.wireOp",EDGE,"E18"),sQuery(id+"F0.wireOp",EDGE,"E19.trimOffspring"),sQuery(id+"F0.wireOp",EDGE,"E20.MirrorC"),sQuery(id+"F0.wireOp",EDGE,"E21.MirrorC"),sQuery(id+"F0.wireOp",EDGE,"E22.MirrorC"),sQuery(id+"F0.wireOp",EDGE,"E24.MirrorC"),sQuery(id+"F0.wireOp",EDGE,"E27.MirrorC"),sQuery(id+"F0.wireOp",EDGE,"E28.MirrorC"),sQuery(id+"F0.wireOp",EDGE,"E29.MirrorCS"),sQuery(id+"F0.wireOp",EDGE,"E30.MirrorCS"),sQuery(id+"F0.wireOp",EDGE,"E35"),sQuery(id+"F0.wireOp",EDGE,"E36"),subQ0,sQuery(id+"F0.wireOp",EDGE,"E38.0"),sQuery(id+"F0.wireOp",EDGE,"E39"),sQuery(id+"F0.wireOp",EDGE,"E40"),sQuery(id+"F0.wireOp",EDGE,"E41"),sQuery(id+"F0.wireOp",EDGE,"E42.trimOffspring"),sQuery(id+"F0.wireOp",EDGE,"E43.trimOffspring"),sQuery(id+"F0.wireOp",EDGE,"E44.trimOffspring"),sQuery(id+"F0.wireOp",EDGE,"E49.trimOffspring"),sQuery(id+"F0.wireOp",EDGE,"E50.trimOffspring"),sQuery(id+"F0.wireOp",EDGE,"E51.trimOffspring"),sQuery(id+"F0.wireOp",EDGE,"E55.filletArc"),sQuery(id+"F0.wireOp",EDGE,"E56.filletArc"),sQuery(id+"F0.wireOp",EDGE,"E57.filletArc"),sQuery(id+"F0.wireOp",EDGE,"E58.filletArc"),sQuery(id+"F0.wireOp",EDGE,"E59.filletArc"),sQuery(id+"F0.wireOp",EDGE,"E60.filletArc")])],"isStart":true})]})}),-1.0]])]});}
            var Q6;
            Q6=sQuery(id+"F6.wireOp",EDGE,"E77.4");
            var Q7;
            Q7=sQuery(id+"F6.wireOp",EDGE,"E77.3");
            var Q8;
            Q8=sQuery(id+"F6.wireOp",EDGE,"E77.2");
            var Q9;
            Q9=sQuery(id+"F6.wireOp",EDGE,"E77.1");
            var Q10;
            Q10=sQuery(id+"F6.wireOp",EDGE,"E77.0");
            var Q11;
            Q11=sQuery(id+"F6.wireOp",EDGE,"E77.5");
            extrude(context, id + "F7", {"entities" : qUnion([Q0, Q1, Q2, Q3, Q4, Q5]), "operationType" : NewBodyOperationType.REMOVE, "surfaceEntities" : qUnion([Q6, Q7, Q8, Q9, Q10, Q11]), "oppositeDirection" : true, "depth" : 3 * mm, "offsetDistance" : 25 * mm});
        }
    });
